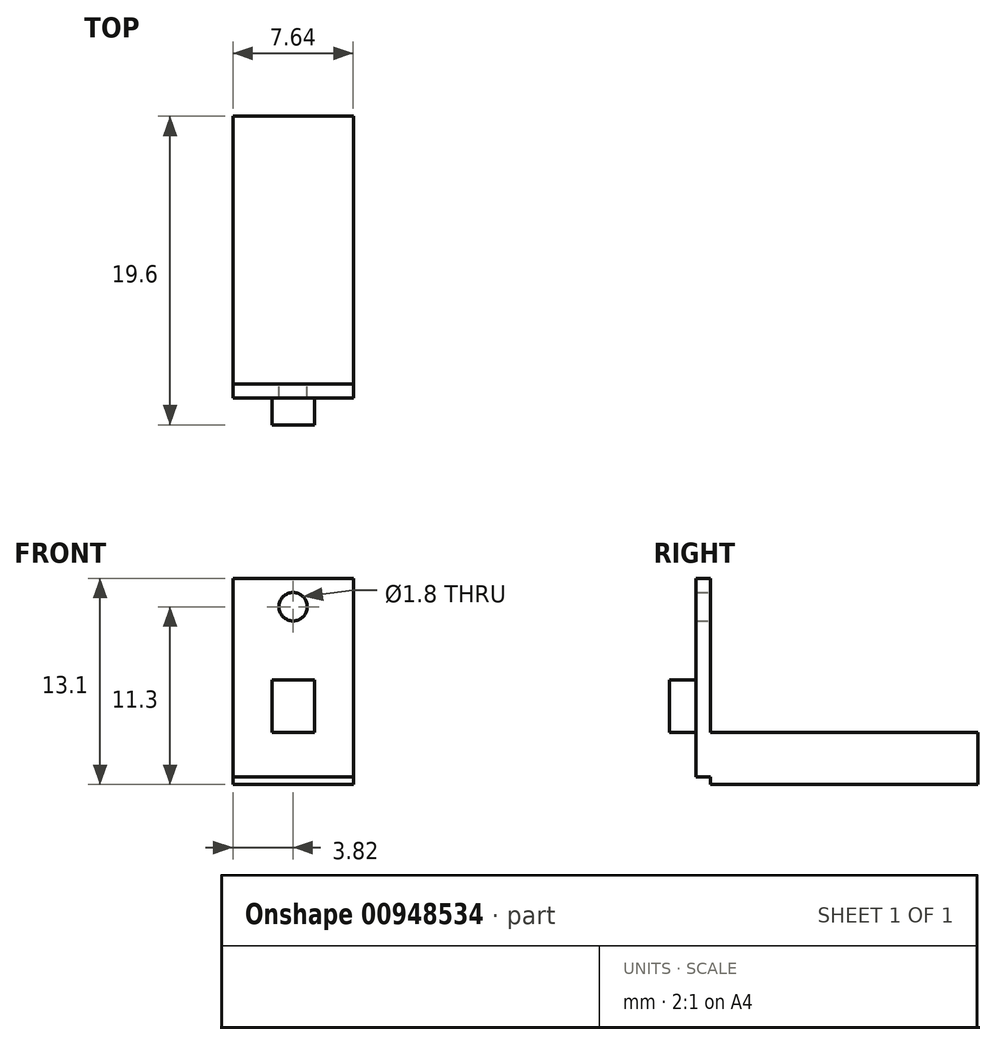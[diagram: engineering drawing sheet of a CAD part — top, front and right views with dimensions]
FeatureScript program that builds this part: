
annotation { "Feature Type Name" : "Feature", "Feature Type Description" : "" }
export const myFeature = defineFeature(function(context is Context, id is Id, definition is map)
    precondition{}
    {
        {
            var Q0;
            Q0=qCreatedBy(makeId("Front.planeOp"),FACE);
            var sketch = newSketch(context, id + "F0", { "sketchPlane" : qUnion([Q0])});
            skLineSegment(sketch, "E0.bottom", {"start": v(-3.82, 1.8) * mm, "end": v(3.82, 1.8) * mm});
            skLineSegment(sketch, "E0.top", {"start": v(-3.82, -10.8) * mm, "end": v(3.83, -10.8) * mm});
            skLineSegment(sketch, "E0.left", {"start": v(-3.82, 1.8) * mm, "end": v(-3.82, -10.8) * mm});
            skLineSegment(sketch, "E0.right", {"start": v(3.83, 1.8) * mm, "end": v(3.83, -10.8) * mm});
            skCircle(sketch, "E1", {"center": v(0, 0) * mm, "radius": 0.9 * mm});
            skPoint(sketch, "E2", {"position": v(0, 1.8) * mm});
            skSolve(sketch);
        }
        {
            var Q0;
            Q0=makeQuery(id+"F0.imprint","IMPRINT",FACE,{"disambiguationData":[TD([[makeQuery(id+"F0.imprint","IMPRINT",EDGE,{"derivedFrom":sQuery(id+"F0.wireOp",EDGE,"E0.bottom")}),-1.0]])]});
            extrude(context, id + "F1", {"entities" : qUnion([Q0]), "depth" : 0.9 * mm, "offsetDistance" : 25 * mm});
        }
        {
            var Q0;
            Q0=makeQuery(id+"F1.opExtrude","CAP_FACE",FACE,{"disambiguationData":[OSD([sQuery(id+"F0.wireOp",EDGE,"E0.bottom"),sQuery(id+"F0.wireOp",EDGE,"E0.top"),sQuery(id+"F0.wireOp",EDGE,"E0.left"),sQuery(id+"F0.wireOp",EDGE,"E0.right"),sQuery(id+"F0.wireOp",EDGE,"E1")])],"isStart":true});
            var sketch = newSketch(context, id + "F2", { "sketchPlane" : qUnion([Q0])});
            skLineSegment(sketch, "E3.bottom", {"start": v(-3.82, -8) * mm, "end": v(3.82, -8) * mm});
            skLineSegment(sketch, "E3.top", {"start": v(-3.82, -11.3) * mm, "end": v(3.82, -11.3) * mm});
            skLineSegment(sketch, "E3.left", {"start": v(-3.82, -8) * mm, "end": v(-3.82, -11.3) * mm});
            skLineSegment(sketch, "E3.right", {"start": v(3.82, -8) * mm, "end": v(3.82, -11.3) * mm});
            skPoint(sketch, "E4", {"position": v(0, -11.3) * mm});
            skSolve(sketch);
        }
        {
            var Q0;
            Q0 = qSketchRegion(id + "F2", true);
            extrude(context, id + "F3", {"entities" : qUnion([Q0]), "operationType" : NewBodyOperationType.ADD, "depth" : 17 * mm, "offsetDistance" : 25 * mm});
        }
        {
            var Q0;
            Q0=makeQuery(id+"F1.opExtrude","CAP_FACE",FACE,{"disambiguationData":[OSD([sQuery(id+"F0.wireOp",EDGE,"E0.bottom"),sQuery(id+"F0.wireOp",EDGE,"E0.top"),sQuery(id+"F0.wireOp",EDGE,"E0.left"),sQuery(id+"F0.wireOp",EDGE,"E0.right"),sQuery(id+"F0.wireOp",EDGE,"E1")])],"isStart":false});
            var sketch = newSketch(context, id + "F4", { "sketchPlane" : qUnion([Q0])});
            skLineSegment(sketch, "E5.bottom", {"start": v(1.35, -4.65) * mm, "end": v(-1.35, -4.65) * mm});
            skLineSegment(sketch, "E5.top", {"start": v(1.35, -8) * mm, "end": v(-1.35, -8) * mm});
            skLineSegment(sketch, "E5.left", {"start": v(1.35, -4.65) * mm, "end": v(1.35, -8) * mm});
            skLineSegment(sketch, "E5.right", {"start": v(-1.35, -4.65) * mm, "end": v(-1.35, -8) * mm});
            skPoint(sketch, "E5.middle", {"position": v(0, -6.33) * mm});
            skSolve(sketch);
        }
        {
            var Q0;
            Q0=makeQuery(id+"F4.imprint","IMPRINT",FACE,{"disambiguationData":[TD([[makeQuery(id+"F4.imprint","IMPRINT",EDGE,{"derivedFrom":sQuery(id+"F4.wireOp",EDGE,"E5.bottom")}),1.0]])]});
            extrude(context, id + "F5", {"entities" : qUnion([Q0]), "operationType" : NewBodyOperationType.ADD, "depth" : 1.7 * mm, "offsetDistance" : 25 * mm});
        }
    });
